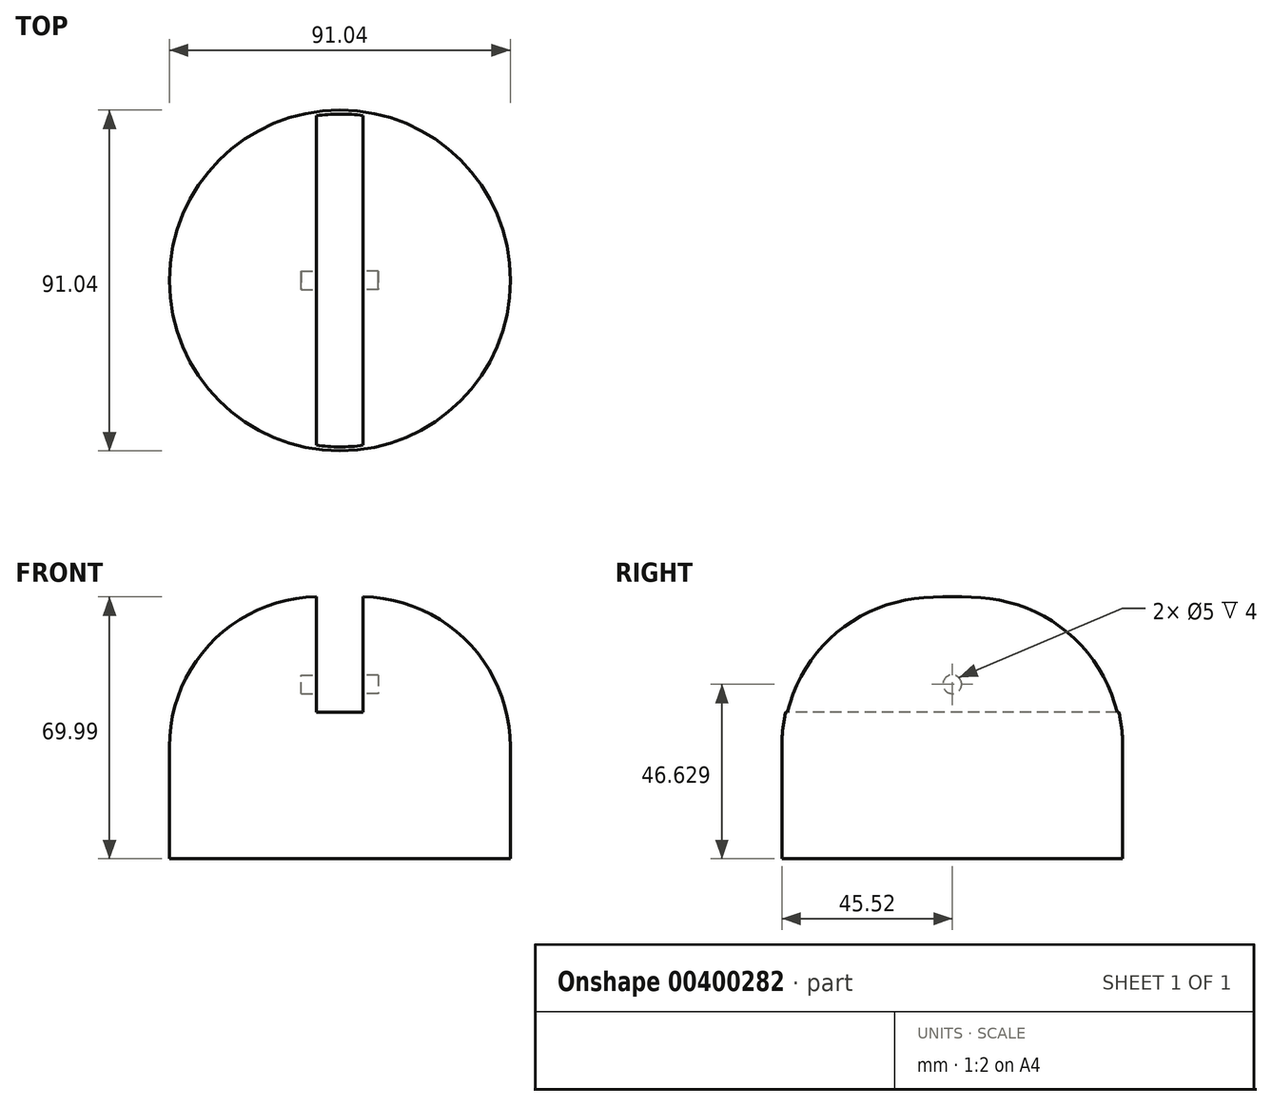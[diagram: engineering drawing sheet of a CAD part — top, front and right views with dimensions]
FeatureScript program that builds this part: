
annotation { "Feature Type Name" : "Feature", "Feature Type Description" : "" }
export const myFeature = defineFeature(function(context is Context, id is Id, definition is map)
    precondition{}
    {
        {
            var Q0;
            Q0=qCreatedBy(makeId("Top.planeOp"),FACE);
            var sketch = newSketch(context, id + "F0", { "sketchPlane" : qUnion([Q0])});
            skCircle(sketch, "E0", {"center": v(0, 0) * mm, "radius": 45.52 * mm});
            skSolve(sketch);
        }
        {
            var Q0;
            Q0=makeQuery(id+"F0.imprint","IMPRINT",FACE,{"disambiguationData":[TD([[makeQuery(id+"F0.imprint","IMPRINT",EDGE,{"derivedFrom":sQuery(id+"F0.wireOp",EDGE,"E0")}),1.0]])]});
            extrude(context, id + "F1", {"entities" : qUnion([Q0]), "depth" : 20 * mm});
        }
        {
            var Q0;
            Q0=makeQuery(id+"F1.opExtrude","CAP_FACE",FACE,{"disambiguationData":[OSD([sQuery(id+"F0.wireOp",EDGE,"E0")])],"isStart":false});
            extrude(context, id + "F2", {"entities" : qUnion([Q0]), "operationType" : NewBodyOperationType.ADD, "depth" : 50 * mm});
        }
        {
            var Q0;
            Q0=makeQuery(id+"F2.opExtrude","CAP_EDGE",EDGE,{"disambiguationData":[OSD([sQuery(id+"F0.wireOp",EDGE,"E0")])],"isStart":false});
            fillet(context, id + "F3", {"entities" : qUnion([Q0]), "radius" : 40 * mm, "allowEdgeOverflow" : false});
        }
        {
            var Q0;
            Q0=qCreatedBy(makeId("Front.planeOp"),FACE);
            var sketch = newSketch(context, id + "F4", { "sketchPlane" : qUnion([Q0])});
            skLineSegment(sketch, "E1.bottom", {"start": v(-6.33, 70.14) * mm, "end": v(6.2, 70.14) * mm});
            skLineSegment(sketch, "E1.top", {"start": v(-6.33, 39.13) * mm, "end": v(6.2, 39.13) * mm});
            skLineSegment(sketch, "E1.left", {"start": v(-6.33, 70.14) * mm, "end": v(-6.33, 39.13) * mm});
            skLineSegment(sketch, "E1.right", {"start": v(6.2, 70.14) * mm, "end": v(6.2, 39.13) * mm});
            skSolve(sketch);
        }
        {
            var Q0;
            Q0 = qSketchRegion(id + "F4", true);
            extrude(context, id + "F5", {"entities" : qUnion([Q0]), "operationType" : NewBodyOperationType.REMOVE, "oppositeDirection" : true, "depth" : 100 * mm});
        }
        {
            var Q0;
            Q0=makeQuery(id+"F5.boolean.opBoolean","COPY",FACE,{"derivedFrom":makeQuery(id+"F5.opExtrude","CAP_FACE",FACE,{"disambiguationData":[OSD([sQuery(id+"F4.wireOp",EDGE,"E1.bottom"),sQuery(id+"F4.wireOp",EDGE,"E1.top"),sQuery(id+"F4.wireOp",EDGE,"E1.left"),sQuery(id+"F4.wireOp",EDGE,"E1.right")])],"isStart":true})});
            var sketch = newSketch(context, id + "F6", { "sketchPlane" : qUnion([Q0])});
            skSolve(sketch);
        }
        {
            var Q0;
            {var subQ2=sQuery(id+"F4.wireOp",EDGE,"E1.top");Q0=makeQuery(id+"F6.imprint","IMPRINT",FACE,{"disambiguationData":[TD([[makeQuery(id+"F6.imprint","IMPRINT",EDGE,{"derivedFrom":makeQuery(id+"F5.boolean.opBoolean","COPY",EDGE,{"derivedFrom":makeQuery(id+"F5.opExtrude","CAP_EDGE",EDGE,{"disambiguationData":[OSD([subQ2])],"isStart":true})})}),-1.0]])]});}
            extrude(context, id + "F7", {"entities" : qUnion([Q0]), "operationType" : NewBodyOperationType.REMOVE, "oppositeDirection" : true, "depth" : 100 * mm});
        }
        {
            var Q0;
            {var subQ0=sQuery(id+"F4.wireOp",EDGE,"E1.left");Q0=makeQuery(id+"F7.boolean.opBoolean","MERGE",FACE,{"derivedFrom":[makeQuery(id+"F5.boolean.opBoolean","COPY",FACE,{"derivedFrom":makeQuery(id+"F5.opExtrude","SWEPT_FACE",FACE,{"disambiguationData":[OSD([subQ0])]})}),makeQuery(id+"F7.opExtrude","SWEPT_FACE",FACE,{"disambiguationData":[OSD([subQ0])]})]});}
            var sketch = newSketch(context, id + "F8", { "sketchPlane" : qUnion([Q0])});
            skCircle(sketch, "E2", {"center": v(0, 46.63) * mm, "radius": 2.5 * mm});
            skSolve(sketch);
        }
        {
            var Q0;
            Q0=makeQuery(id+"F8.imprint","IMPRINT",FACE,{"disambiguationData":[TD([[makeQuery(id+"F8.imprint","IMPRINT",EDGE,{"derivedFrom":sQuery(id+"F8.wireOp",EDGE,"E2")}),1.0]])]});
            var Q1;
            Q1=sQuery(id+"F8.wireOp",EDGE,"E2");
            extrude(context, id + "F9", {"entities" : qUnion([Q0]), "operationType" : NewBodyOperationType.REMOVE, "surfaceEntities" : qUnion([Q1]), "oppositeDirection" : true, "depth" : 4 * mm});
        }
        {
            var Q0;
            {var subQ0=sQuery(id+"F4.wireOp",EDGE,"E1.right");Q0=makeQuery(id+"F7.boolean.opBoolean","MERGE",FACE,{"derivedFrom":[makeQuery(id+"F5.boolean.opBoolean","COPY",FACE,{"derivedFrom":makeQuery(id+"F5.opExtrude","SWEPT_FACE",FACE,{"disambiguationData":[OSD([subQ0])]})}),makeQuery(id+"F7.opExtrude","SWEPT_FACE",FACE,{"disambiguationData":[OSD([subQ0])]})]});}
            var sketch = newSketch(context, id + "F10", { "sketchPlane" : qUnion([Q0])});
            skCircle(sketch, "E3", {"center": v(0, 46.63) * mm, "radius": 2.5 * mm});
            skSolve(sketch);
        }
        {
            var Q0;
            Q0 = qSketchRegion(id + "F10", true);
            extrude(context, id + "F11", {"entities" : qUnion([Q0]), "operationType" : NewBodyOperationType.REMOVE, "oppositeDirection" : true, "depth" : 4 * mm});
        }
    });
